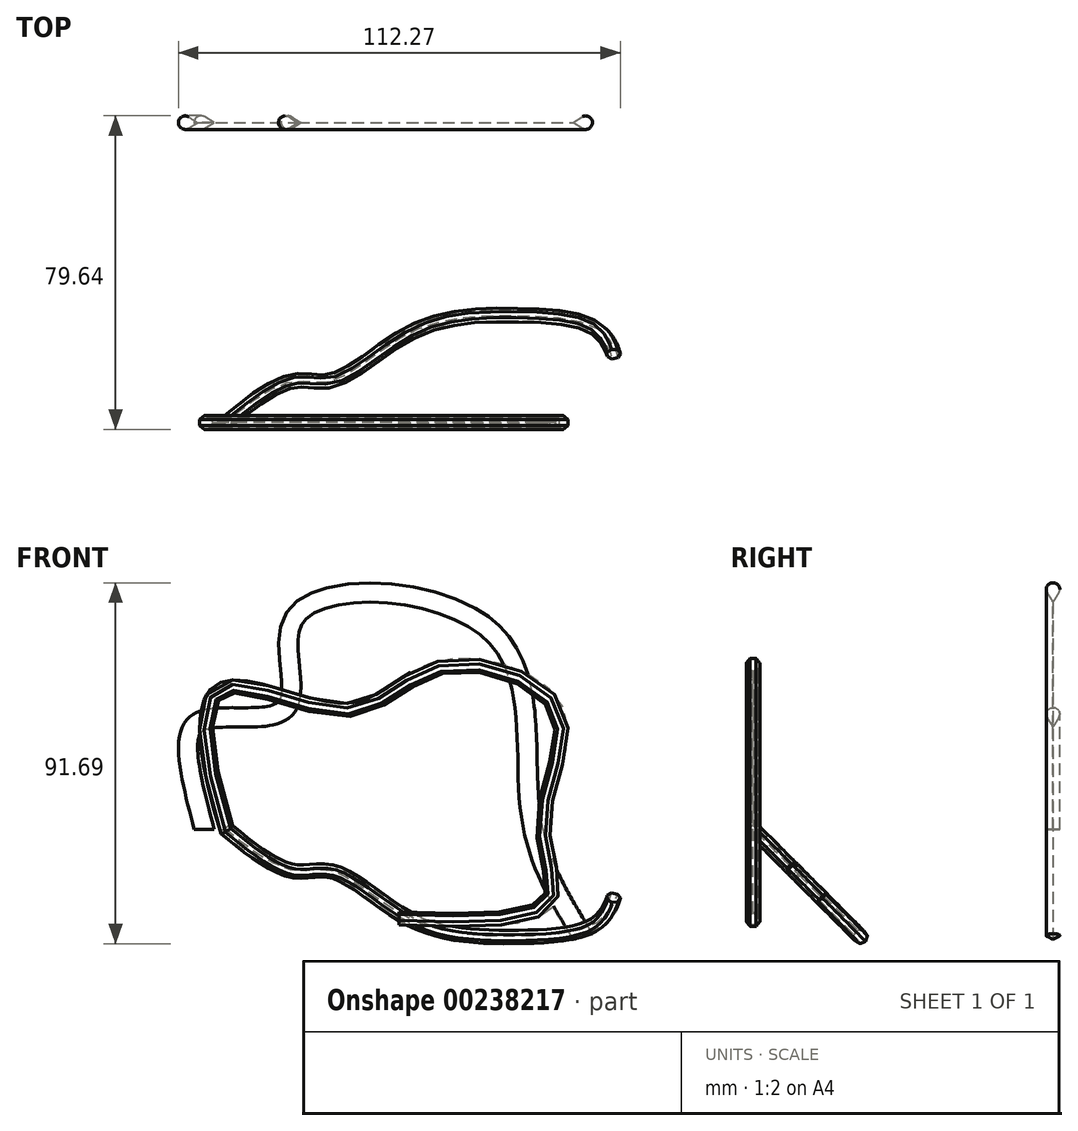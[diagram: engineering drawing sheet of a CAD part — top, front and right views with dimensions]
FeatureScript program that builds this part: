
annotation { "Feature Type Name" : "Feature", "Feature Type Description" : "" }
export const myFeature = defineFeature(function(context is Context, id is Id, definition is map)
    precondition{}
    {
        {
            var Q0;
            Q0=qCreatedBy(makeId("Front.planeOp"),FACE);
            var sketch = newSketch(context, id + "F0", { "sketchPlane" : qUnion([Q0])});
            skFitSpline(sketch, "E0", {"points": [v(-50.36, 0) * mm, v(-50.66, 28.17) * mm, v(-29.4, 31.46) * mm, v(-27, 54.45) * mm, v(23.5, 51.24) * mm, v(34.01, 5.4) * mm, v(47.44, -27) * mm], "startDerivative": vector(-76.03, 294.33) * mm, "endDerivative": vector(112.62, -184.44) * mm});
            skSolve(sketch);
        }
        {
            var Q0;
            Q0=qCreatedBy(makeId("Top.planeOp"),FACE);
            var sketch = newSketch(context, id + "F1", { "sketchPlane" : qUnion([Q0])});
            skArc(sketch, "E1", {"start": v(-49.47, 1.47) * mm, "mid": v(-52.08, 0.02) * mm, "end": v(-49.5, -1.49) * mm});
            skLineSegment(sketch, "E2", {"start": v(-49.5, -1.49) * mm, "end": v(-47, -0.03) * mm});
            skLineSegment(sketch, "E3", {"start": v(-47, -0.03) * mm, "end": v(-49.47, 1.47) * mm});
            skSolve(sketch);
        }
        {
            var Q0;
            Q0=makeQuery(id+"F1.imprint","IMPRINT",FACE,{"disambiguationData":[TD([[makeQuery(id+"F1.imprint","IMPRINT",EDGE,{"derivedFrom":sQuery(id+"F1.wireOp",EDGE,"E1")}),1.0]])]});
            var Q1;
            Q1=sQuery(id+"F0.wireOp",EDGE,"E0");
            sweep(context, id + "F2", {"profiles" : qUnion([Q0]), "path" : qUnion([Q1])});
        }
        {
            var Q0;
            Q0=qCreatedBy(makeId("Front.planeOp"),FACE);
            cPlane(context, id + "F3", {"entities" : qUnion([Q0]), "cplaneType" : CPlaneType.OFFSET, "offset" : 76.2 * mm, "width" : 152.4 * mm, "height" : 152.4 * mm});
        }
        {
            var Q0;
            Q0=qCreatedBy(id+"F3.planeOp",FACE);
            var sketch = newSketch(context, id + "F4", { "sketchPlane" : qUnion([Q0])});
            skFitSpline(sketch, "E4", {"points": [v(-43.9, 0) * mm, v(-44.77, 35.9) * mm, v(-13.02, 30.45) * mm, v(10.85, 41.33) * mm, v(40.32, 30.1) * mm, v(36.64, 1.5) * mm, v(38.22, -18.15) * mm, v(0, -22.71) * mm], "startDerivative": vector(-107.48, 338.86) * mm, "endDerivative": vector(-321.26, 11.32) * mm});
            skSolve(sketch);
        }
        {
            var Q0;
            Q0=qCreatedBy(makeId("Top.planeOp"),FACE);
            var Q1;
            Q1=qCreatedBy(id+"F3.planeOp",FACE);
            cPlane(context, id + "F5", {"entities" : qUnion([Q0, Q1]), "cplaneType" : CPlaneType.MID_PLANE, "offset" : 25.4 * mm, "width" : 152.4 * mm, "height" : 152.4 * mm});
        }
        {
            var Q0;
            Q0=qCreatedBy(id+"F5.planeOp",FACE);
            var sketch = newSketch(context, id + "F6", { "sketchPlane" : qUnion([Q0])});
            skPoint(sketch, "E5.0", {"position": v(43.9, 53.88) * mm});
            skFitSpline(sketch, "E6", {"points": [v(43.9, 53.88) * mm, v(26.87, 38.96) * mm, v(16.98, 38.78) * mm, v(-3.86, 20.87) * mm, v(-29.79, 15.3) * mm, v(-50.6, 20.64) * mm, v(-54.45, 29.27) * mm], "startDerivative": vector(-88.15, -103.2) * mm, "endDerivative": vector(-2.25, 17.9) * mm});
            skSolve(sketch);
        }
        {
            var Q0;
            Q0=qCreatedBy(makeId("Right.planeOp"),FACE);
            var sketch = newSketch(context, id + "F7", { "sketchPlane" : qUnion([Q0])});
            skPoint(sketch, "E7.0", {"position": v(-76.2, -22.71) * mm});
            skCircle(sketch, "E8.cCircle", {"center": v(-76.2, -22.71) * mm, "radius": 1.59 * mm, "construction": true});
            skLineSegment(sketch, "E8.0", {"start": v(-75.44, -24.3) * mm, "end": v(-76.96, -24.3) * mm});
            skLineSegment(sketch, "E8.1", {"start": v(-76.96, -24.3) * mm, "end": v(-77.92, -23.1) * mm});
            skLineSegment(sketch, "E8.2", {"start": v(-77.92, -23.1) * mm, "end": v(-77.58, -21.61) * mm});
            skLineSegment(sketch, "E8.3", {"start": v(-77.58, -21.61) * mm, "end": v(-76.2, -20.95) * mm});
            skLineSegment(sketch, "E8.4", {"start": v(-76.2, -20.95) * mm, "end": v(-74.82, -21.61) * mm});
            skLineSegment(sketch, "E8.5", {"start": v(-74.82, -21.61) * mm, "end": v(-74.48, -23.1) * mm});
            skLineSegment(sketch, "E8.6", {"start": v(-74.48, -23.1) * mm, "end": v(-75.44, -24.3) * mm});
            skPoint(sketch, "E8.0.midPoint", {"position": v(-76.2, -24.3) * mm});
            skSolve(sketch);
        }
        {
            var Q0;
            Q0=makeQuery(id+"F7.imprint","IMPRINT",FACE,{"disambiguationData":[TD([[makeQuery(id+"F7.imprint","IMPRINT",EDGE,{"derivedFrom":sQuery(id+"F7.wireOp",EDGE,"E8.0")}),-1.0]])]});
            var Q1;
            Q1=sQuery(id+"F4.wireOp",EDGE,"E4");
            var Q2;
            Q2=sQuery(id+"F6.wireOp",EDGE,"E6");
            sweep(context, id + "F8", {"profiles" : qUnion([Q0]), "path" : qUnion([Q1, Q2])});
        }
    });
